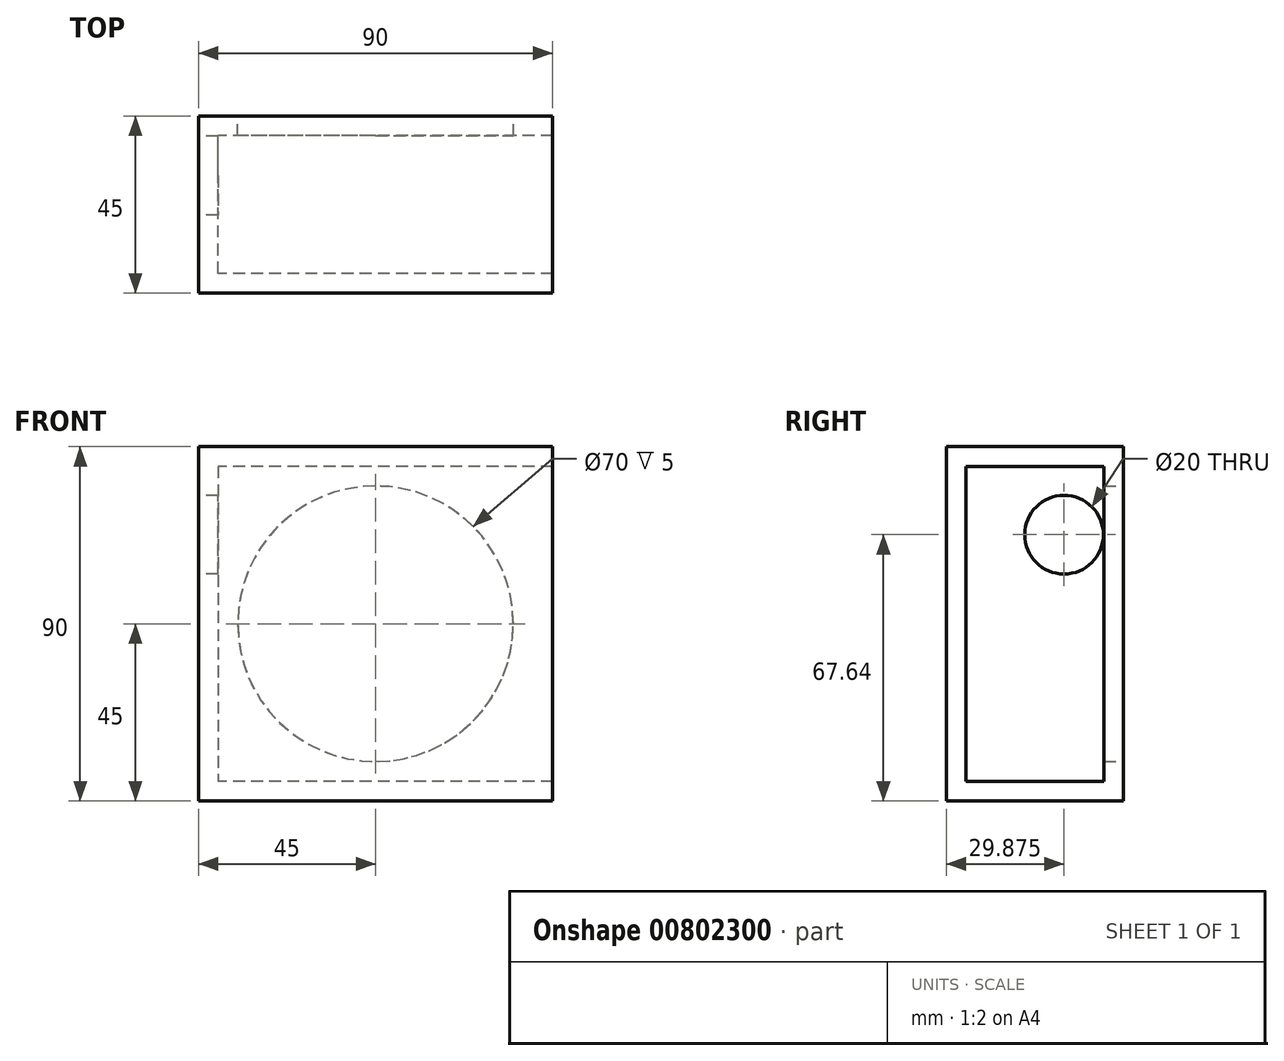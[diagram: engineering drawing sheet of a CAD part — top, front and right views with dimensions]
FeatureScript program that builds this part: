
annotation { "Feature Type Name" : "Feature", "Feature Type Description" : "" }
export const myFeature = defineFeature(function(context is Context, id is Id, definition is map)
    precondition{}
    {
        {
            var Q0;
            Q0=qCreatedBy(makeId("Front.planeOp"),FACE);
            var sketch = newSketch(context, id + "F0", { "sketchPlane" : qUnion([Q0])});
            skLineSegment(sketch, "E0.bottom", {"start": v(45, 45) * mm, "end": v(-45, 45) * mm});
            skLineSegment(sketch, "E0.top", {"start": v(45, -45) * mm, "end": v(-45, -45) * mm});
            skLineSegment(sketch, "E0.left", {"start": v(45, 45) * mm, "end": v(45, -45) * mm});
            skLineSegment(sketch, "E0.right", {"start": v(-45, 45) * mm, "end": v(-45, -45) * mm});
            skPoint(sketch, "E0.middle", {"position": v(0, 0) * mm});
            skSolve(sketch);
        }
        {
            var Q0;
            Q0=makeQuery(id+"F0.imprint","IMPRINT",FACE,{"disambiguationData":[TD([[makeQuery(id+"F0.imprint","IMPRINT",EDGE,{"derivedFrom":sQuery(id+"F0.wireOp",EDGE,"E0.bottom")}),1.0]])]});
            extrude(context, id + "F1", {"entities" : qUnion([Q0]), "depth" : 45 * mm, "offsetDistance" : 25 * mm});
        }
        {
            var Q0;
            Q0=makeQuery(id+"F1.opExtrude","SWEPT_FACE",FACE,{"disambiguationData":[OSD([sQuery(id+"F0.wireOp",EDGE,"E0.left")])]});
            shell(context, id + "F2", {"entities" : qUnion([Q0]), "thickness" : 5 * mm});
        }
        {
            var Q0;
            Q0=sQuery(id+"F0.wireOp",VERTEX,"E0.middle");
            var Q1;
            Q1=makeQuery(id+"F1.opExtrude","SWEPT_BODY",BODY,{"disambiguationData":[OSD([sQuery(id+"F0.wireOp",EDGE,"E0.bottom"),sQuery(id+"F0.wireOp",EDGE,"E0.top"),sQuery(id+"F0.wireOp",EDGE,"E0.left"),sQuery(id+"F0.wireOp",EDGE,"E0.right")])]});
            hole(context, id + "F3", {"style" : HoleStyle.SIMPLE, "endStyle" : HoleEndStyle.BLIND, "oppositeDirection" : true, "holeDiameter" : 70 * mm, "majorDiameter" : 5 * mm, "holeDepth" : 10 * mm, "isTappedThrough" : true, "tappedDepth" : 12 * mm, "tapClearance" : 3, "locations" : qUnion([Q0]), "scope" : qUnion([Q1])});
        }
        {
            var Q0;
            Q0=makeQuery(id+"F1.opExtrude","SWEPT_FACE",FACE,{"disambiguationData":[OSD([sQuery(id+"F0.wireOp",EDGE,"E0.right")])]});
            var sketch = newSketch(context, id + "F4", { "sketchPlane" : qUnion([Q0])});
            skSolve(sketch);
        }
        {
            var Q0;
            {var subQ0=sQuery(id+"F0.wireOp",EDGE,"E0.right");Q0=makeQuery(id+"F4.imprint","IMPRINT",FACE,{"disambiguationData":[TD([[makeQuery(id+"F4.imprint","IMPRINT",EDGE,{"derivedFrom":makeQuery(id+"F1.opExtrude","CAP_EDGE",EDGE,{"disambiguationData":[OSD([subQ0])],"isStart":true})}),1.0]])]});}
            var sketch = newSketch(context, id + "F5", { "sketchPlane" : qUnion([Q0])});
            skCircle(sketch, "E1", {"center": v(15.12, 22.64) * mm, "radius": 10 * mm});
            skSolve(sketch);
        }
        {
            var Q0;
            Q0=sQuery(id+"F5.wireOp",VERTEX,"E1.center");
            var Q1;
            Q1=makeQuery(id+"F1.opExtrude","SWEPT_BODY",BODY,{"disambiguationData":[OSD([sQuery(id+"F0.wireOp",EDGE,"E0.bottom"),sQuery(id+"F0.wireOp",EDGE,"E0.top"),sQuery(id+"F0.wireOp",EDGE,"E0.left"),sQuery(id+"F0.wireOp",EDGE,"E0.right")])]});
            hole(context, id + "F6", {"style" : HoleStyle.SIMPLE, "endStyle" : HoleEndStyle.BLIND, "holeDiameter" : 20 * mm, "majorDiameter" : 5 * mm, "holeDepth" : 12 * mm, "isTappedThrough" : true, "tappedDepth" : 12 * mm, "tapClearance" : 3, "locations" : qUnion([Q0]), "scope" : qUnion([Q1])});
        }
    });
